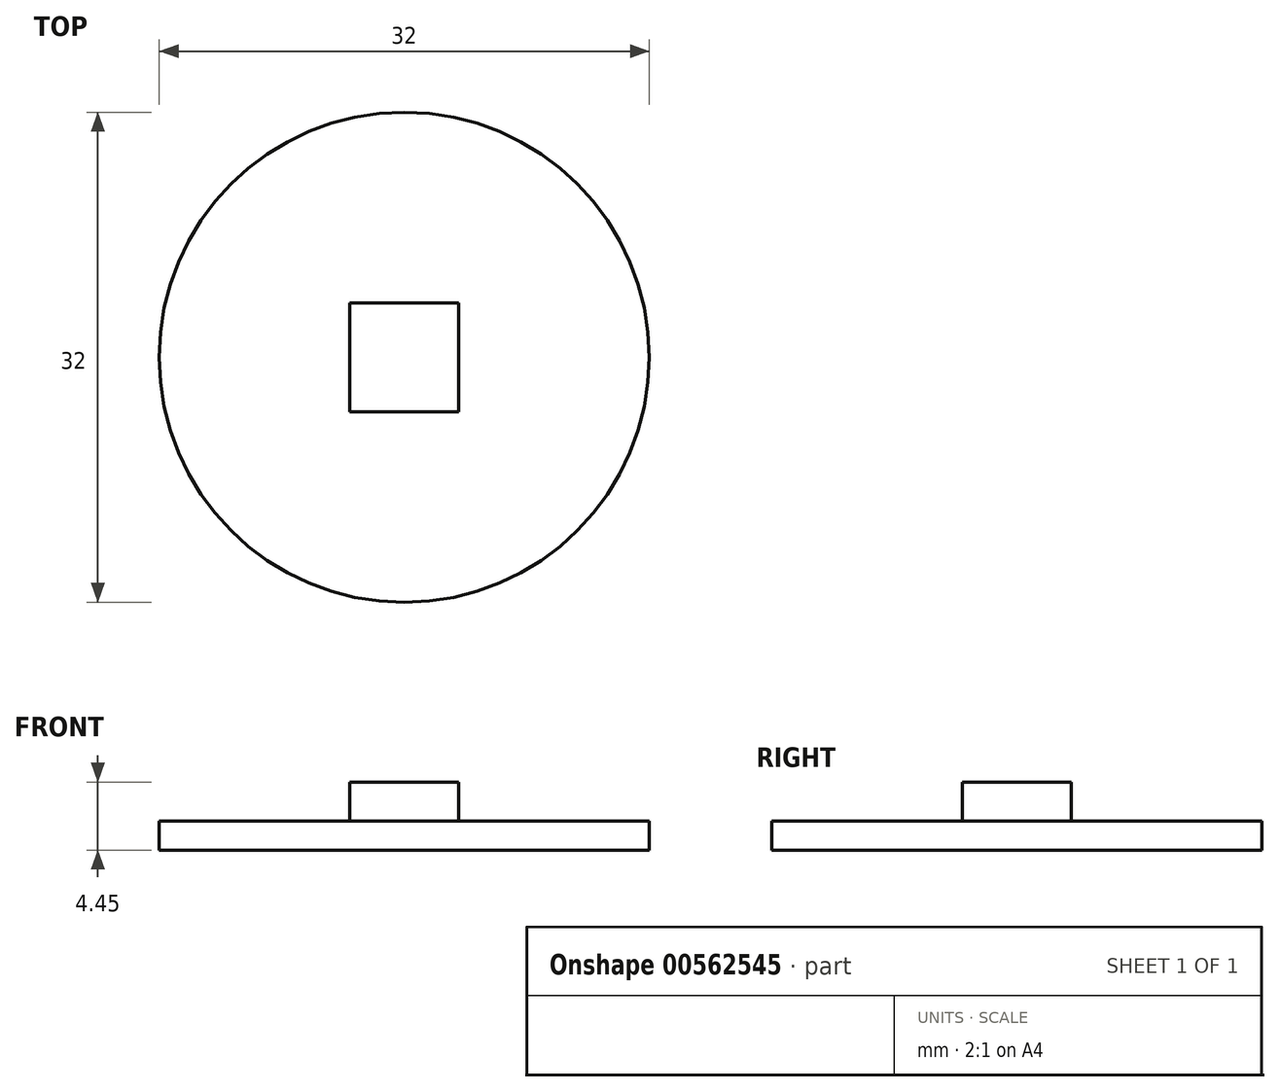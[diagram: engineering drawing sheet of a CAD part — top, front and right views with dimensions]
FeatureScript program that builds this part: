
annotation { "Feature Type Name" : "Feature", "Feature Type Description" : "" }
export const myFeature = defineFeature(function(context is Context, id is Id, definition is map)
    precondition{}
    {
        {
            var Q0;
            Q0=qCreatedBy(makeId("Top.planeOp"),FACE);
            var sketch = newSketch(context, id + "F0", { "sketchPlane" : qUnion([Q0])});
            skCircle(sketch, "E0", {"center": v(0, 0) * mm, "radius": 16 * mm});
            skSolve(sketch);
        }
        {
            var Q0;
            Q0=makeQuery(id+"F0.imprint","IMPRINT",FACE,{"disambiguationData":[TD([[makeQuery(id+"F0.imprint","IMPRINT",EDGE,{"derivedFrom":sQuery(id+"F0.wireOp",EDGE,"E0")}),1.0]])]});
            extrude(context, id + "F1", {"entities" : qUnion([Q0]), "depth" : 1.9 * mm, "offsetDistance" : 25.4 * mm});
        }
        {
            var Q0;
            Q0=makeQuery(id+"F1.opExtrude","CAP_FACE",FACE,{"disambiguationData":[OSD([sQuery(id+"F0.wireOp",EDGE,"E0")])],"isStart":false});
            var sketch = newSketch(context, id + "F2", { "sketchPlane" : qUnion([Q0])});
            skPoint(sketch, "E1", {"position": v(0, 0) * mm});
            skLineSegment(sketch, "E2", {"start": v(0, 0) * mm, "end": v(0, 14.36) * mm, "construction": true});
            skLineSegment(sketch, "E3", {"start": v(0, 0) * mm, "end": v(14.71, 0) * mm, "construction": true});
            skLineSegment(sketch, "E4", {"start": v(3.56, 0) * mm, "end": v(3.56, 13.94) * mm, "construction": true});
            skLineSegment(sketch, "E5", {"start": v(0, 3.56) * mm, "end": v(22.95, 3.56) * mm, "construction": true});
            skLineSegment(sketch, "E6.bottom", {"start": v(3.56, 3.56) * mm, "end": v(-3.56, 3.56) * mm});
            skLineSegment(sketch, "E6.top", {"start": v(3.56, -3.56) * mm, "end": v(-3.56, -3.56) * mm});
            skLineSegment(sketch, "E6.left", {"start": v(3.56, 3.56) * mm, "end": v(3.56, -3.56) * mm});
            skLineSegment(sketch, "E6.right", {"start": v(-3.56, 3.56) * mm, "end": v(-3.56, -3.56) * mm});
            skSolve(sketch);
        }
        {
            var Q0;
            Q0=makeQuery(id+"F2.imprint","IMPRINT",FACE,{"disambiguationData":[TD([[makeQuery(id+"F2.imprint","IMPRINT",EDGE,{"derivedFrom":sQuery(id+"F2.wireOp",EDGE,"E6.bottom")}),1.0]])]});
            extrude(context, id + "F3", {"entities" : qUnion([Q0]), "depth" : 2.54 * mm, "offsetDistance" : 25.4 * mm});
        }
    });
